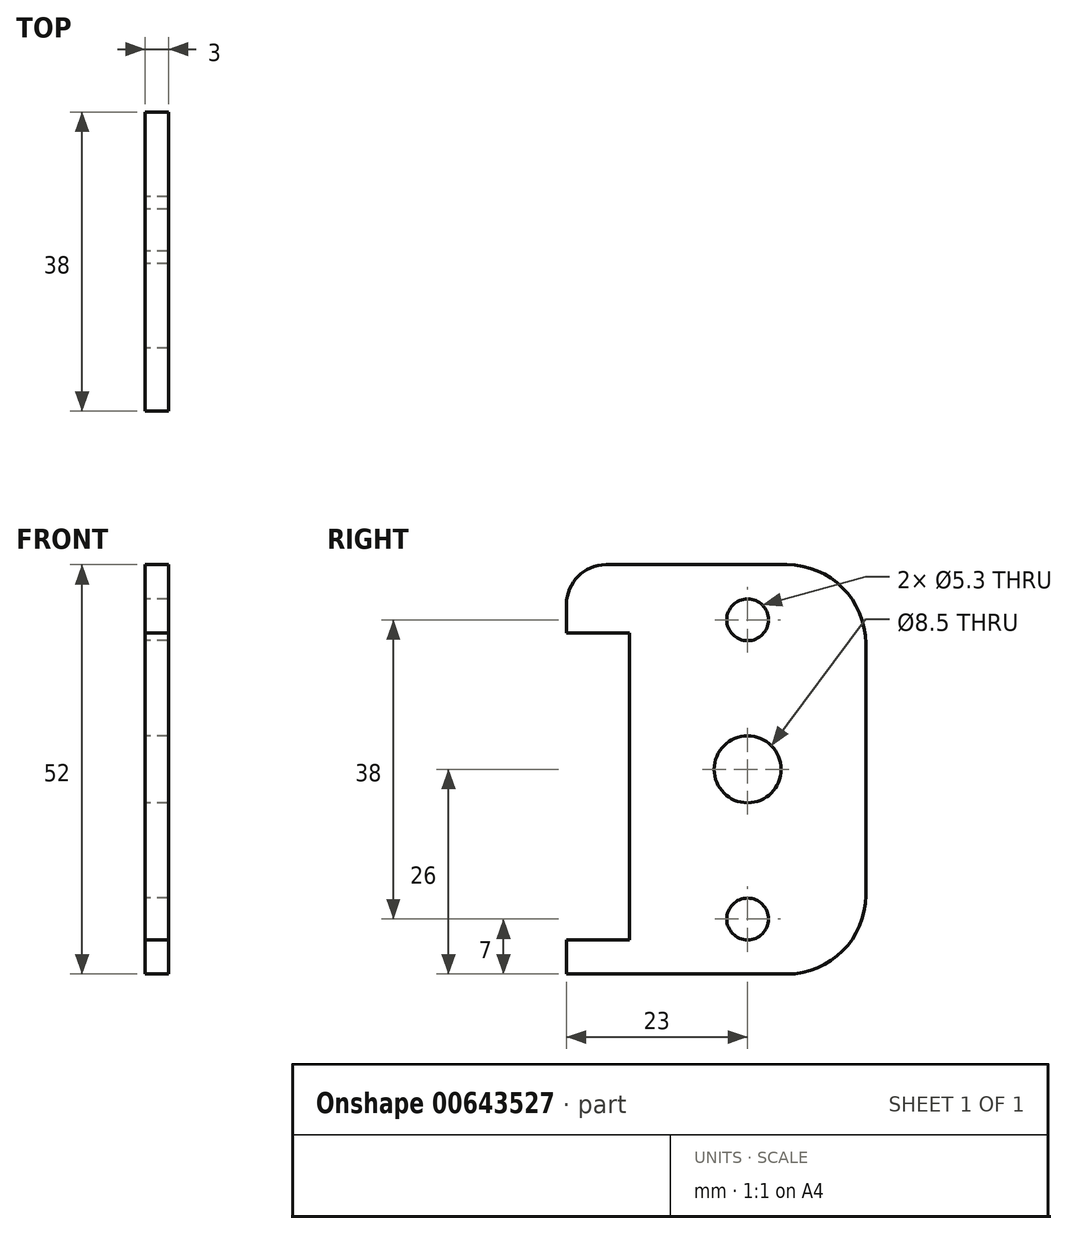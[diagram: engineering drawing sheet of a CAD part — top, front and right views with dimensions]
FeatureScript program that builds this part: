
annotation { "Feature Type Name" : "Feature", "Feature Type Description" : "" }
export const myFeature = defineFeature(function(context is Context, id is Id, definition is map)
    precondition{}
    {
        {
            var Q0;
            Q0=qCreatedBy(makeId("Right.planeOp"),FACE);
            var sketch = newSketch(context, id + "F0", { "sketchPlane" : qUnion([Q0])});
            skLineSegment(sketch, "E0.bottom", {"start": v(19, 26) * mm, "end": v(-19, 26) * mm, "construction": true});
            skLineSegment(sketch, "E0.top", {"start": v(19, -26) * mm, "end": v(-19, -26) * mm, "construction": true});
            skLineSegment(sketch, "E0.left", {"start": v(19, 26) * mm, "end": v(19, -26) * mm, "construction": true});
            skLineSegment(sketch, "E0.right", {"start": v(-19, 26) * mm, "end": v(-19, -26) * mm, "construction": true});
            skPoint(sketch, "E0.middle", {"position": v(0, 0) * mm});
            skLineSegment(sketch, "E1", {"start": v(-19, 21) * mm, "end": v(-19, 17.3) * mm});
            skLineSegment(sketch, "E2", {"start": v(-19, 17.3) * mm, "end": v(-11, 17.3) * mm});
            skLineSegment(sketch, "E3", {"start": v(-11, 17.3) * mm, "end": v(-11, -21.65) * mm});
            skLineSegment(sketch, "E4", {"start": v(-11, -21.65) * mm, "end": v(-19, -21.65) * mm});
            skLineSegment(sketch, "E5", {"start": v(-19, -21.65) * mm, "end": v(-19, -26) * mm});
            skLineSegment(sketch, "E6", {"start": v(19, -16) * mm, "end": v(19, 16) * mm});
            skLineSegment(sketch, "E7", {"start": v(9, 26) * mm, "end": v(-14, 26) * mm});
            skLineSegment(sketch, "E8", {"start": v(-19, -26) * mm, "end": v(9, -26) * mm});
            skPoint(sketch, "E9.visualSharp", {"position": v(19, 26) * mm});
            skArc(sketch, "E9.filletArc", {"start": v(19, 16) * mm, "mid": v(16.07, 23.07) * mm, "end": v(9, 26) * mm});
            skPoint(sketch, "E10.visualSharp", {"position": v(19, -26) * mm});
            skArc(sketch, "E10.filletArc", {"start": v(9, -26) * mm, "mid": v(16.07, -23.07) * mm, "end": v(19, -16) * mm});
            skCircle(sketch, "E11", {"center": v(4, 19) * mm, "radius": 2.65 * mm});
            skCircle(sketch, "E12", {"center": v(4, -19) * mm, "radius": 2.65 * mm});
            skLineSegment(sketch, "E13", {"start": v(4, -19) * mm, "end": v(4, 19) * mm, "construction": true});
            skCircle(sketch, "E14", {"center": v(4, 0) * mm, "radius": 4.25 * mm});
            skCircle(sketch, "E15", {"center": v(4, 19) * mm, "radius": 4.97 * mm, "construction": true});
            skCircle(sketch, "E16", {"center": v(4, -19) * mm, "radius": 4.97 * mm, "construction": true});
            skCircle(sketch, "E17", {"center": v(4, 0) * mm, "radius": 4.97 * mm, "construction": true});
            skCircle(sketch, "E18", {"center": v(4, 0) * mm, "radius": 10.97 * mm, "construction": true});
            skPoint(sketch, "E19.visualSharp", {"position": v(-19, 26) * mm});
            skArc(sketch, "E19.filletArc", {"start": v(-14, 26) * mm, "mid": v(-17.54, 24.54) * mm, "end": v(-19, 21) * mm});
            skSolve(sketch);
        }
        {
            var Q0;
            Q0 = qSketchRegion(id + "F0", true);
            extrude(context, id + "F1", {"entities" : qUnion([Q0]), "depth" : 3 * mm, "offsetDistance" : 25 * mm});
        }
    });
